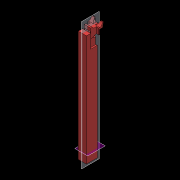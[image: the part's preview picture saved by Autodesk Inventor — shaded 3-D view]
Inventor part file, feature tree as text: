
AUTODESK INVENTOR PART (.ipt)
format: ipt  version: 2018.2 (Build 222227000, 227)  size: 804,864 bytes
history: native  units: mm
features: other x5, mirror x1
ambient origin geometry x8: Origin, YZ Plane, XZ Plane, XY Plane, X Axis, Y Axis, Z Axis, Center Point
bodies: Body1 (feature_tree), Body2 (feature_tree)
feature tree (6):
  other  "ソリッド1"
  other  "作業平面1"
  other  "作業平面2"
  other  "ソリッド2"
  mirror  "Mirror2"
  other  "CrvPattern1"
